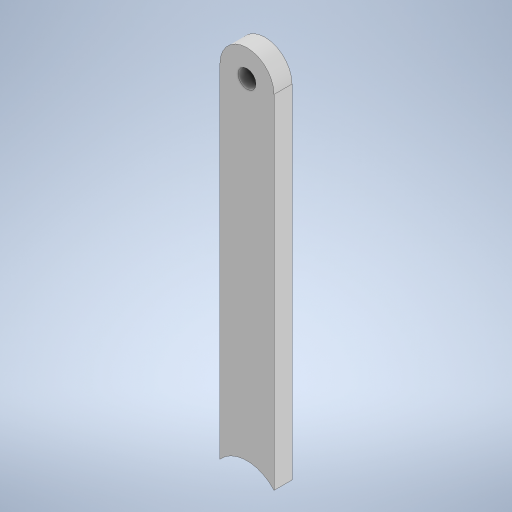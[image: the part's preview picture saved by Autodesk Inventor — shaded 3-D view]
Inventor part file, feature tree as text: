
AUTODESK INVENTOR PART (.ipt)
format: ipt  version: 2023 (Build 270158000, 158)  size: 232,960 bytes
history: native  units: in
note: dims shown in document units (in); Inventor stores cm internally (conversion verified against a paired STEP export)
features: extrude x1, sketch x1
ambient origin geometry x8: Origin, YZ Plane, XZ Plane, XY Plane, X Axis, Y Axis, Z Axis, Center Point
bodies: Solid1 (feature_tree)
feature tree (2):
  extrude  "Extrusion1"  Depth=0.0312in
  sketch  "Sketch1"  dims[d4=0.683in d5=0.125in d6=0.0312in d7=0.0in]
